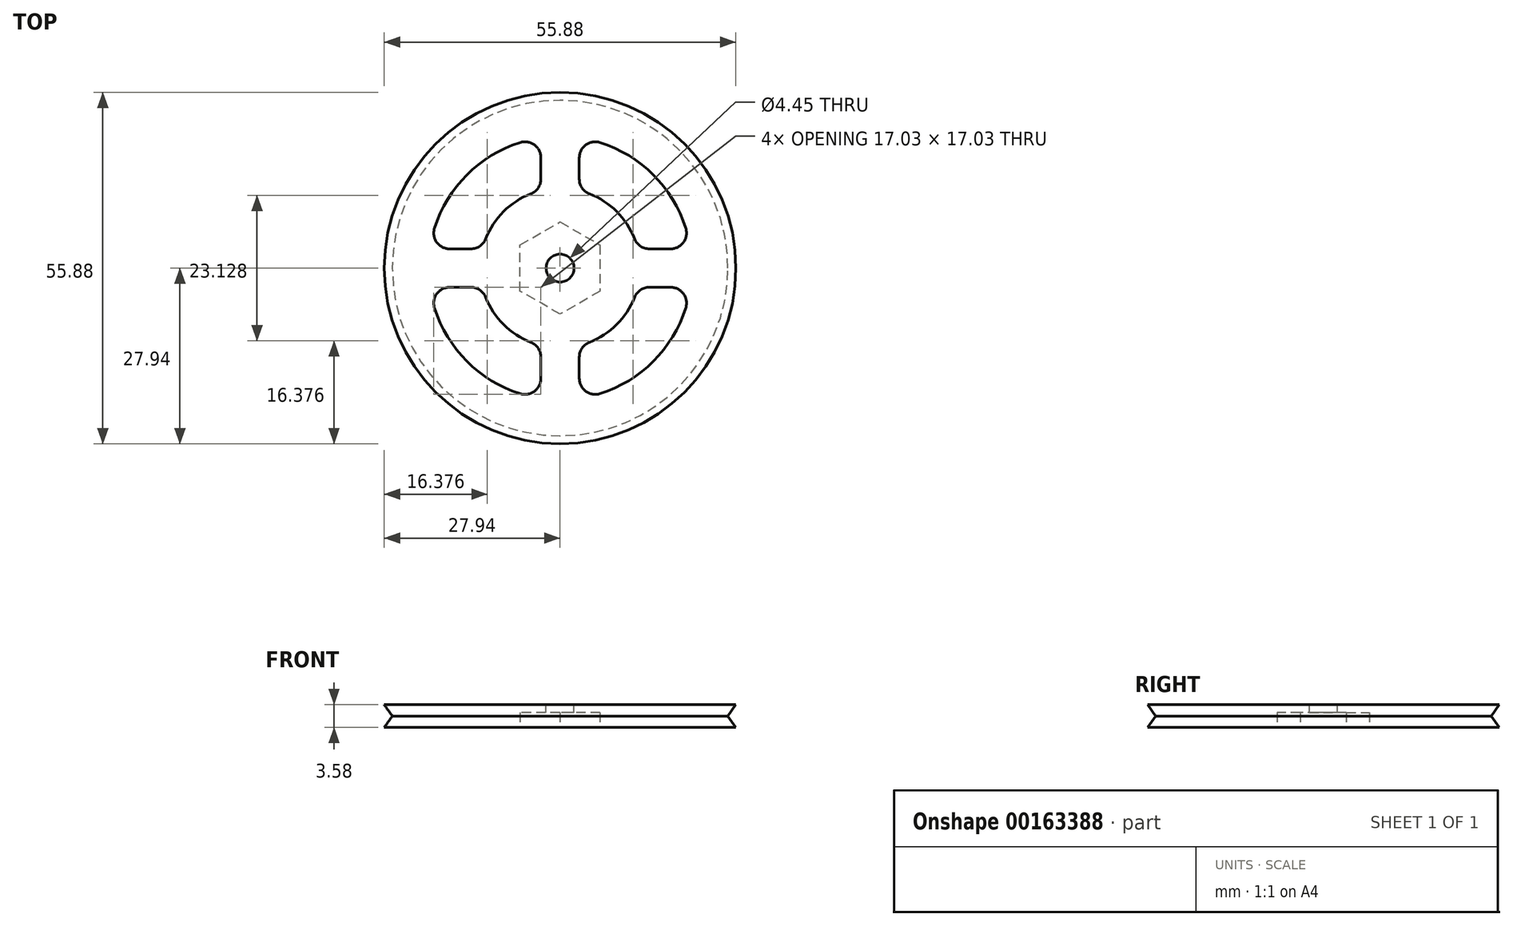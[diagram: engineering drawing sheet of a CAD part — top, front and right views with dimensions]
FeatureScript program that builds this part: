
annotation { "Feature Type Name" : "Feature", "Feature Type Description" : "" }
export const myFeature = defineFeature(function(context is Context, id is Id, definition is map)
    precondition{}
    {
        {
            var Q0;
            Q0=qCreatedBy(makeId("Top.planeOp"),FACE);
            var sketch = newSketch(context, id + "F0", { "sketchPlane" : qUnion([Q0])});
            skCircle(sketch, "E0", {"center": v(0, 0) * mm, "radius": 27.94 * mm});
            skCircle(sketch, "E1.cCircle", {"center": v(0, 0) * mm, "radius": 6.35 * mm, "construction": true});
            skLineSegment(sketch, "E1.0", {"start": v(6.35, -3.67) * mm, "end": v(0, -7.33) * mm});
            skLineSegment(sketch, "E1.1", {"start": v(0, -7.33) * mm, "end": v(-6.35, -3.67) * mm});
            skLineSegment(sketch, "E1.2", {"start": v(-6.35, -3.67) * mm, "end": v(-6.35, 3.67) * mm});
            skLineSegment(sketch, "E1.3", {"start": v(-6.35, 3.67) * mm, "end": v(0, 7.33) * mm});
            skLineSegment(sketch, "E1.4", {"start": v(0, 7.33) * mm, "end": v(6.35, 3.67) * mm});
            skLineSegment(sketch, "E1.5", {"start": v(6.35, 3.67) * mm, "end": v(6.35, -3.67) * mm});
            skPoint(sketch, "E1.0.midPoint", {"position": v(3.18, -5.5) * mm});
            skArc(sketch, "E2", {"start": v(-4.66, 11.82) * mm, "mid": v(-8.98, 8.98) * mm, "end": v(-11.82, 4.66) * mm});
            skArc(sketch, "E3", {"start": v(-6.36, 19.97) * mm, "mid": v(-14.82, 14.82) * mm, "end": v(-19.97, 6.36) * mm});
            skLineSegment(sketch, "E4", {"start": v(-3.05, 17.55) * mm, "end": v(-3.05, 14.18) * mm});
            skLineSegment(sketch, "E5", {"start": v(3.05, 17.55) * mm, "end": v(3.05, 14.18) * mm});
            skLineSegment(sketch, "E6", {"start": v(-17.55, 3.05) * mm, "end": v(-14.18, 3.05) * mm});
            skLineSegment(sketch, "E7", {"start": v(-17.55, -3.05) * mm, "end": v(-14.18, -3.05) * mm});
            skLineSegment(sketch, "E8", {"start": v(3.05, -14.18) * mm, "end": v(3.05, -17.55) * mm});
            skLineSegment(sketch, "E9", {"start": v(14.18, 3.05) * mm, "end": v(17.55, 3.05) * mm});
            skLineSegment(sketch, "E10", {"start": v(14.18, -3.05) * mm, "end": v(17.55, -3.05) * mm});
            skLineSegment(sketch, "E11", {"start": v(-3.05, -14.18) * mm, "end": v(-3.05, -17.55) * mm});
            skArc(sketch, "E12.trimOffspring", {"start": v(-11.82, -4.66) * mm, "mid": v(-8.98, -8.98) * mm, "end": v(-4.66, -11.82) * mm});
            skArc(sketch, "E13.trimOffspring", {"start": v(-19.97, -6.36) * mm, "mid": v(-14.82, -14.82) * mm, "end": v(-6.36, -19.97) * mm});
            skArc(sketch, "E14.trimOffspring", {"start": v(6.36, -19.97) * mm, "mid": v(14.82, -14.82) * mm, "end": v(19.97, -6.36) * mm});
            skArc(sketch, "E15.trimOffspring", {"start": v(4.66, -11.82) * mm, "mid": v(8.98, -8.98) * mm, "end": v(11.82, -4.66) * mm});
            skArc(sketch, "E16.trimOffspring", {"start": v(11.82, 4.66) * mm, "mid": v(8.98, 8.98) * mm, "end": v(4.66, 11.82) * mm});
            skArc(sketch, "E17.trimOffspring", {"start": v(19.97, 6.36) * mm, "mid": v(14.82, 14.82) * mm, "end": v(6.36, 19.97) * mm});
            skPoint(sketch, "E18.visualSharp", {"position": v(-3.05, 20.73) * mm});
            skArc(sketch, "E18.filletArc", {"start": v(-3.05, 17.55) * mm, "mid": v(-4.09, 19.6) * mm, "end": v(-6.36, 19.97) * mm});
            skPoint(sketch, "E19.visualSharp", {"position": v(-3.05, 12.33) * mm});
            skArc(sketch, "E19.filletArc", {"start": v(-4.66, 11.82) * mm, "mid": v(-3.49, 12.75) * mm, "end": v(-3.05, 14.18) * mm});
            skPoint(sketch, "E20.visualSharp", {"position": v(-12.33, 3.05) * mm});
            skArc(sketch, "E20.filletArc", {"start": v(-14.18, 3.05) * mm, "mid": v(-12.75, 3.49) * mm, "end": v(-11.82, 4.66) * mm});
            skPoint(sketch, "E21.visualSharp", {"position": v(-20.73, 3.05) * mm});
            skArc(sketch, "E21.filletArc", {"start": v(-19.97, 6.36) * mm, "mid": v(-19.6, 4.09) * mm, "end": v(-17.55, 3.05) * mm});
            skPoint(sketch, "E22.visualSharp", {"position": v(-12.33, -3.05) * mm});
            skArc(sketch, "E22.filletArc", {"start": v(-11.82, -4.66) * mm, "mid": v(-12.75, -3.49) * mm, "end": v(-14.18, -3.05) * mm});
            skPoint(sketch, "E23.visualSharp", {"position": v(-20.73, -3.05) * mm});
            skArc(sketch, "E23.filletArc", {"start": v(-17.55, -3.05) * mm, "mid": v(-19.6, -4.09) * mm, "end": v(-19.97, -6.36) * mm});
            skPoint(sketch, "E24.visualSharp", {"position": v(-3.05, -12.33) * mm});
            skArc(sketch, "E24.filletArc", {"start": v(-3.05, -14.18) * mm, "mid": v(-3.49, -12.75) * mm, "end": v(-4.66, -11.82) * mm});
            skPoint(sketch, "E25.visualSharp", {"position": v(-3.05, -20.73) * mm});
            skArc(sketch, "E25.filletArc", {"start": v(-6.36, -19.97) * mm, "mid": v(-4.09, -19.6) * mm, "end": v(-3.05, -17.55) * mm});
            skPoint(sketch, "E26.visualSharp", {"position": v(3.05, -12.33) * mm});
            skArc(sketch, "E26.filletArc", {"start": v(4.66, -11.82) * mm, "mid": v(3.49, -12.75) * mm, "end": v(3.05, -14.18) * mm});
            skPoint(sketch, "E27.visualSharp", {"position": v(3.05, -20.73) * mm});
            skArc(sketch, "E27.filletArc", {"start": v(3.05, -17.55) * mm, "mid": v(4.09, -19.6) * mm, "end": v(6.36, -19.97) * mm});
            skPoint(sketch, "E28.visualSharp", {"position": v(20.73, -3.05) * mm});
            skArc(sketch, "E28.filletArc", {"start": v(19.97, -6.36) * mm, "mid": v(19.6, -4.09) * mm, "end": v(17.55, -3.05) * mm});
            skPoint(sketch, "E29.visualSharp", {"position": v(3.05, 12.33) * mm});
            skArc(sketch, "E29.filletArc", {"start": v(3.05, 14.18) * mm, "mid": v(3.49, 12.75) * mm, "end": v(4.66, 11.82) * mm});
            skPoint(sketch, "E30.visualSharp", {"position": v(3.05, 20.73) * mm});
            skArc(sketch, "E30.filletArc", {"start": v(6.36, 19.97) * mm, "mid": v(4.09, 19.6) * mm, "end": v(3.05, 17.55) * mm});
            skPoint(sketch, "E31.visualSharp", {"position": v(12.33, -3.05) * mm});
            skArc(sketch, "E31.filletArc", {"start": v(14.18, -3.05) * mm, "mid": v(12.75, -3.49) * mm, "end": v(11.82, -4.66) * mm});
            skPoint(sketch, "E32.visualSharp", {"position": v(12.33, 3.05) * mm});
            skArc(sketch, "E32.filletArc", {"start": v(11.82, 4.66) * mm, "mid": v(12.75, 3.49) * mm, "end": v(14.18, 3.05) * mm});
            skPoint(sketch, "E33.visualSharp", {"position": v(20.73, 3.05) * mm});
            skArc(sketch, "E33.filletArc", {"start": v(17.55, 3.05) * mm, "mid": v(19.6, 4.09) * mm, "end": v(19.97, 6.36) * mm});
            skSolve(sketch);
        }
        {
            var Q0;
            Q0 = qSketchRegion(id + "F0", true);
            extrude(context, id + "F1", {"entities" : qUnion([Q0]), "endBound" : BoundingType.SYMMETRIC, "depth" : 3.58 * mm});
        }
        {
            var Q0;
            Q0=qCreatedBy(makeId("Right.planeOp"),FACE);
            var sketch = newSketch(context, id + "F2", { "sketchPlane" : qUnion([Q0])});
            skLineSegment(sketch, "E34", {"start": v(26.67, 0) * mm, "end": v(27.94, 1.8) * mm});
            skLineSegment(sketch, "E35", {"start": v(26.67, 0) * mm, "end": v(27.94, -1.8) * mm});
            skLineSegment(sketch, "E36", {"start": v(0, 11.92) * mm, "end": v(0, -11.13) * mm, "construction": true});
            skLineSegment(sketch, "E37", {"start": v(27.94, 1.8) * mm, "end": v(27.94, -1.8) * mm});
            skSolve(sketch);
        }
        {
            var Q0;
            Q0 = qSketchRegion(id + "F2", true);
            var Q1;
            Q1=sQuery(id+"F2.wireOp",EDGE,"E36");
            revolve(context, id + "F3", {"operationType" : NewBodyOperationType.REMOVE, "entities" : qUnion([Q0]), "axis" : qUnion([Q1]), "revolveType" : RevolveType.FULL, "oppositeDirection" : true});
        }
        {
            var Q0;
            Q0=makeQuery(id+"F1.opExtrude","CAP_FACE",FACE,{"disambiguationData":[OSD([sQuery(id+"F0.wireOp",EDGE,"E0"),sQuery(id+"F0.wireOp",EDGE,"E1.0"),sQuery(id+"F0.wireOp",EDGE,"E1.1"),sQuery(id+"F0.wireOp",EDGE,"E1.2"),sQuery(id+"F0.wireOp",EDGE,"E1.3"),sQuery(id+"F0.wireOp",EDGE,"E1.4"),sQuery(id+"F0.wireOp",EDGE,"E1.5"),sQuery(id+"F0.wireOp",EDGE,"E2"),sQuery(id+"F0.wireOp",EDGE,"E3"),sQuery(id+"F0.wireOp",EDGE,"E4"),sQuery(id+"F0.wireOp",EDGE,"E5"),sQuery(id+"F0.wireOp",EDGE,"E6"),sQuery(id+"F0.wireOp",EDGE,"E7"),sQuery(id+"F0.wireOp",EDGE,"E8"),sQuery(id+"F0.wireOp",EDGE,"E9"),sQuery(id+"F0.wireOp",EDGE,"E10"),sQuery(id+"F0.wireOp",EDGE,"E11"),sQuery(id+"F0.wireOp",EDGE,"E12.trimOffspring"),sQuery(id+"F0.wireOp",EDGE,"E13.trimOffspring"),sQuery(id+"F0.wireOp",EDGE,"E14.trimOffspring"),sQuery(id+"F0.wireOp",EDGE,"E15.trimOffspring"),sQuery(id+"F0.wireOp",EDGE,"E16.trimOffspring"),sQuery(id+"F0.wireOp",EDGE,"E17.trimOffspring"),sQuery(id+"F0.wireOp",EDGE,"E18.filletArc"),sQuery(id+"F0.wireOp",EDGE,"E19.filletArc"),sQuery(id+"F0.wireOp",EDGE,"E20.filletArc"),sQuery(id+"F0.wireOp",EDGE,"E21.filletArc"),sQuery(id+"F0.wireOp",EDGE,"E22.filletArc"),sQuery(id+"F0.wireOp",EDGE,"E23.filletArc"),sQuery(id+"F0.wireOp",EDGE,"E24.filletArc"),sQuery(id+"F0.wireOp",EDGE,"E25.filletArc"),sQuery(id+"F0.wireOp",EDGE,"E26.filletArc"),sQuery(id+"F0.wireOp",EDGE,"E27.filletArc"),sQuery(id+"F0.wireOp",EDGE,"E28.filletArc"),sQuery(id+"F0.wireOp",EDGE,"E29.filletArc"),sQuery(id+"F0.wireOp",EDGE,"E30.filletArc"),sQuery(id+"F0.wireOp",EDGE,"E31.filletArc"),sQuery(id+"F0.wireOp",EDGE,"E32.filletArc"),sQuery(id+"F0.wireOp",EDGE,"E33.filletArc")])],"isStart":false});
            var sketch = newSketch(context, id + "F4", { "sketchPlane" : qUnion([Q0])});
            skLineSegment(sketch, "E38", {"start": v(0, 7.33) * mm, "end": v(-6.35, 3.67) * mm});
            skLineSegment(sketch, "E39", {"start": v(-6.35, 3.67) * mm, "end": v(-6.35, -3.67) * mm});
            skLineSegment(sketch, "E40", {"start": v(-6.35, -3.67) * mm, "end": v(0, -7.33) * mm});
            skLineSegment(sketch, "E41", {"start": v(0, -7.33) * mm, "end": v(6.35, -3.67) * mm});
            skLineSegment(sketch, "E42", {"start": v(6.35, -3.67) * mm, "end": v(6.35, 3.67) * mm});
            skLineSegment(sketch, "E43", {"start": v(6.35, 3.67) * mm, "end": v(0, 7.33) * mm});
            skCircle(sketch, "E44", {"center": v(0, 0) * mm, "radius": 2.22 * mm});
            skSolve(sketch);
        }
        {
            var Q0;
            Q0 = qSketchRegion(id + "F4", true);
            extrude(context, id + "F5", {"entities" : qUnion([Q0]), "operationType" : NewBodyOperationType.ADD, "oppositeDirection" : true, "depth" : 1.27 * mm});
        }
    });
